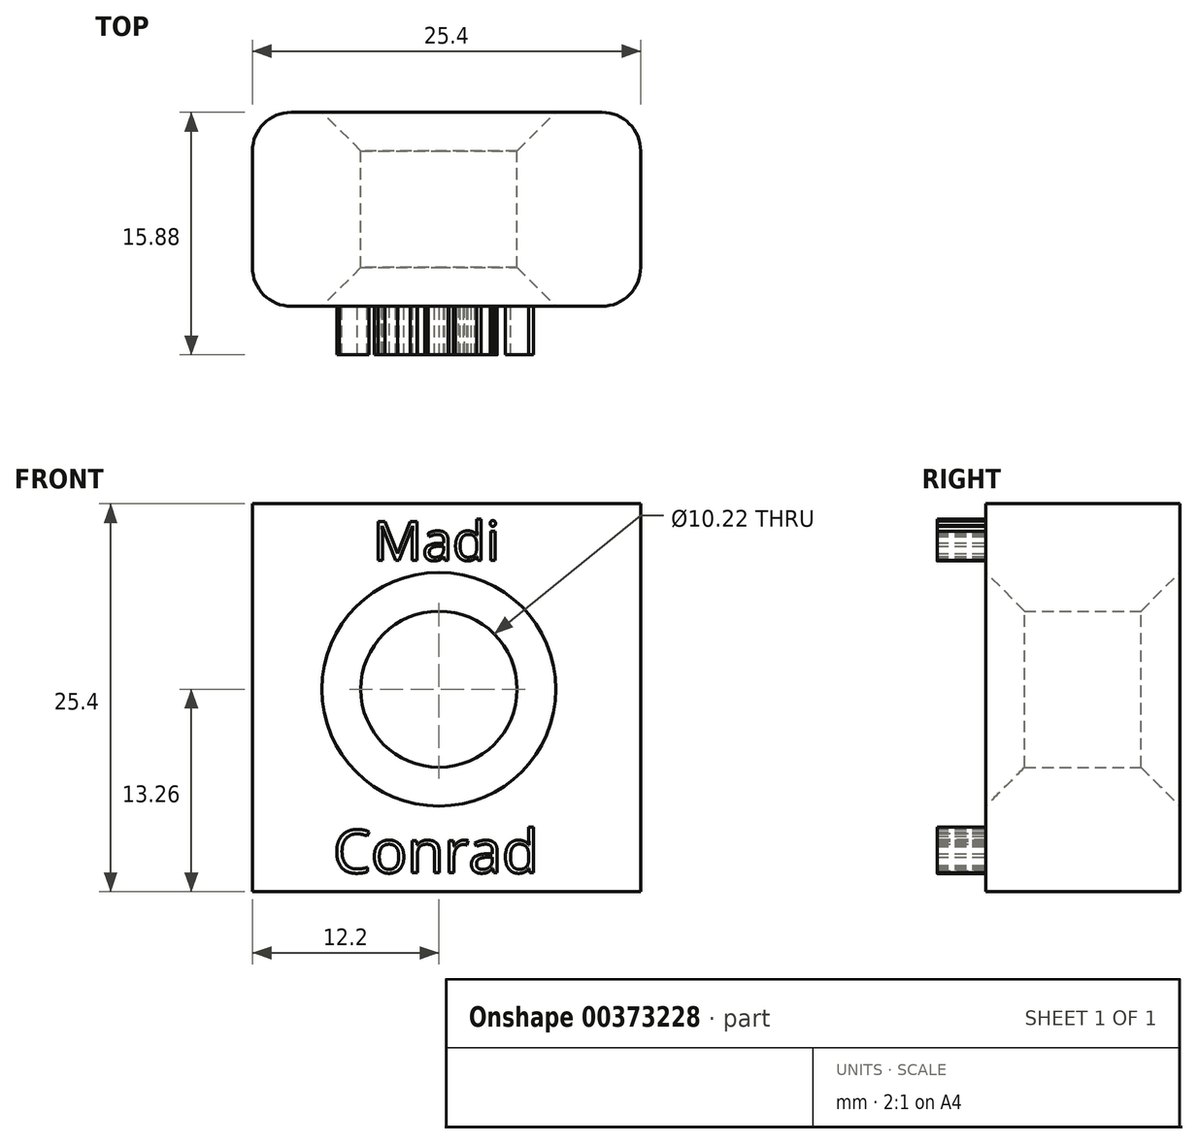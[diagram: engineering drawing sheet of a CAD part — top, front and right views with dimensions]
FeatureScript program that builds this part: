
annotation { "Feature Type Name" : "Feature", "Feature Type Description" : "" }
export const myFeature = defineFeature(function(context is Context, id is Id, definition is map)
    precondition{}
    {
        {
            var Q0;
            Q0=qCreatedBy(makeId("Front.planeOp"),FACE);
            var sketch = newSketch(context, id + "F0", { "sketchPlane" : qUnion([Q0])});
            skLineSegment(sketch, "E0.bottom", {"start": v(7.52, 12.14) * mm, "end": v(32.92, 12.14) * mm});
            skLineSegment(sketch, "E0.top", {"start": v(7.52, -13.26) * mm, "end": v(32.92, -13.26) * mm});
            skLineSegment(sketch, "E0.left", {"start": v(7.52, 12.14) * mm, "end": v(7.52, -13.26) * mm});
            skLineSegment(sketch, "E0.right", {"start": v(32.92, 12.14) * mm, "end": v(32.92, -13.26) * mm});
            skCircle(sketch, "E1", {"center": v(19.72, 0) * mm, "radius": 5.11 * mm});
            skSolve(sketch);
        }
        {
            var Q0;
            Q0=makeQuery(id+"F0.imprint","IMPRINT",FACE,{"disambiguationData":[TD([[makeQuery(id+"F0.imprint","IMPRINT",EDGE,{"derivedFrom":sQuery(id+"F0.wireOp",EDGE,"E0.bottom")}),-1.0]])]});
            extrude(context, id + "F1", {"entities" : qUnion([Q0]), "depth" : 12.7 * mm});
        }
        {
            var Q0;
            Q0=makeQuery(id+"F1.opExtrude","CAP_FACE",FACE,{"disambiguationData":[OSD([sQuery(id+"F0.wireOp",EDGE,"E0.bottom"),sQuery(id+"F0.wireOp",EDGE,"E0.top"),sQuery(id+"F0.wireOp",EDGE,"E0.left"),sQuery(id+"F0.wireOp",EDGE,"E0.right"),sQuery(id+"F0.wireOp",EDGE,"E1")])],"isStart":false});
            var sketch = newSketch(context, id + "F2", { "sketchPlane" : qUnion([Q0])});
            skText(sketch, "E2", { "text": "Madi", "fontName": "OpenSans-Regular.ttf"});
            skText(sketch, "E3", { "text": "Conrad", "fontName": "OpenSans-Regular.ttf"});
            const initialGuessF2  = {"E2": [0.0154, 0.00843, 1, 0, 0.00257], "E3": [0.01279, -0.01202, 1, 0, 0.00283]};
            skSetInitialGuess(sketch, initialGuessF2);
            skSolve(sketch);
        }
        {
            var Q0;
            Q0 = qSketchRegion(id + "F2", true);
            extrude(context, id + "F3", {"entities" : qUnion([Q0]), "operationType" : NewBodyOperationType.ADD, "depth" : 3.17 * mm});
        }
        {
            var Q0;
            Q0=makeQuery(id+"F1.opExtrude","CAP_EDGE",EDGE,{"disambiguationData":[OSD([sQuery(id+"F0.wireOp",EDGE,"E0.right")])],"isStart":false});
            fillet(context, id + "F4", {"entities" : qUnion([Q0]), "radius" : 2.54 * mm, "tangentPropagation" : true, "allowEdgeOverflow" : false});
        }
        {
            var Q0;
            Q0=makeQuery(id+"F1.opExtrude","CAP_EDGE",EDGE,{"disambiguationData":[OSD([sQuery(id+"F0.wireOp",EDGE,"E0.right")])],"isStart":true});
            var Q1;
            Q1=makeQuery(id+"F1.opExtrude","CAP_EDGE",EDGE,{"disambiguationData":[OSD([sQuery(id+"F0.wireOp",EDGE,"E0.left")])],"isStart":true});
            var Q2;
            Q2=makeQuery(id+"F1.opExtrude","CAP_EDGE",EDGE,{"disambiguationData":[OSD([sQuery(id+"F0.wireOp",EDGE,"E0.left")])],"isStart":false});
            fillet(context, id + "F5", {"entities" : qUnion([Q0, Q1, Q2]), "radius" : 2.54 * mm, "tangentPropagation" : true, "allowEdgeOverflow" : false});
        }
        {
            var Q0;
            Q0=makeQuery(id+"F1.opExtrude","CAP_EDGE",EDGE,{"disambiguationData":[OSD([sQuery(id+"F0.wireOp",EDGE,"E1")])],"isStart":false});
            var Q1;
            Q1=makeQuery(id+"F1.opExtrude","CAP_EDGE",EDGE,{"disambiguationData":[OSD([sQuery(id+"F0.wireOp",EDGE,"E1")])],"isStart":true});
            chamfer(context, id + "F6", {"entities" : qUnion([Q0, Q1]), "width" : 2.54 * mm, "tangentPropagation" : true});
        }
    });
